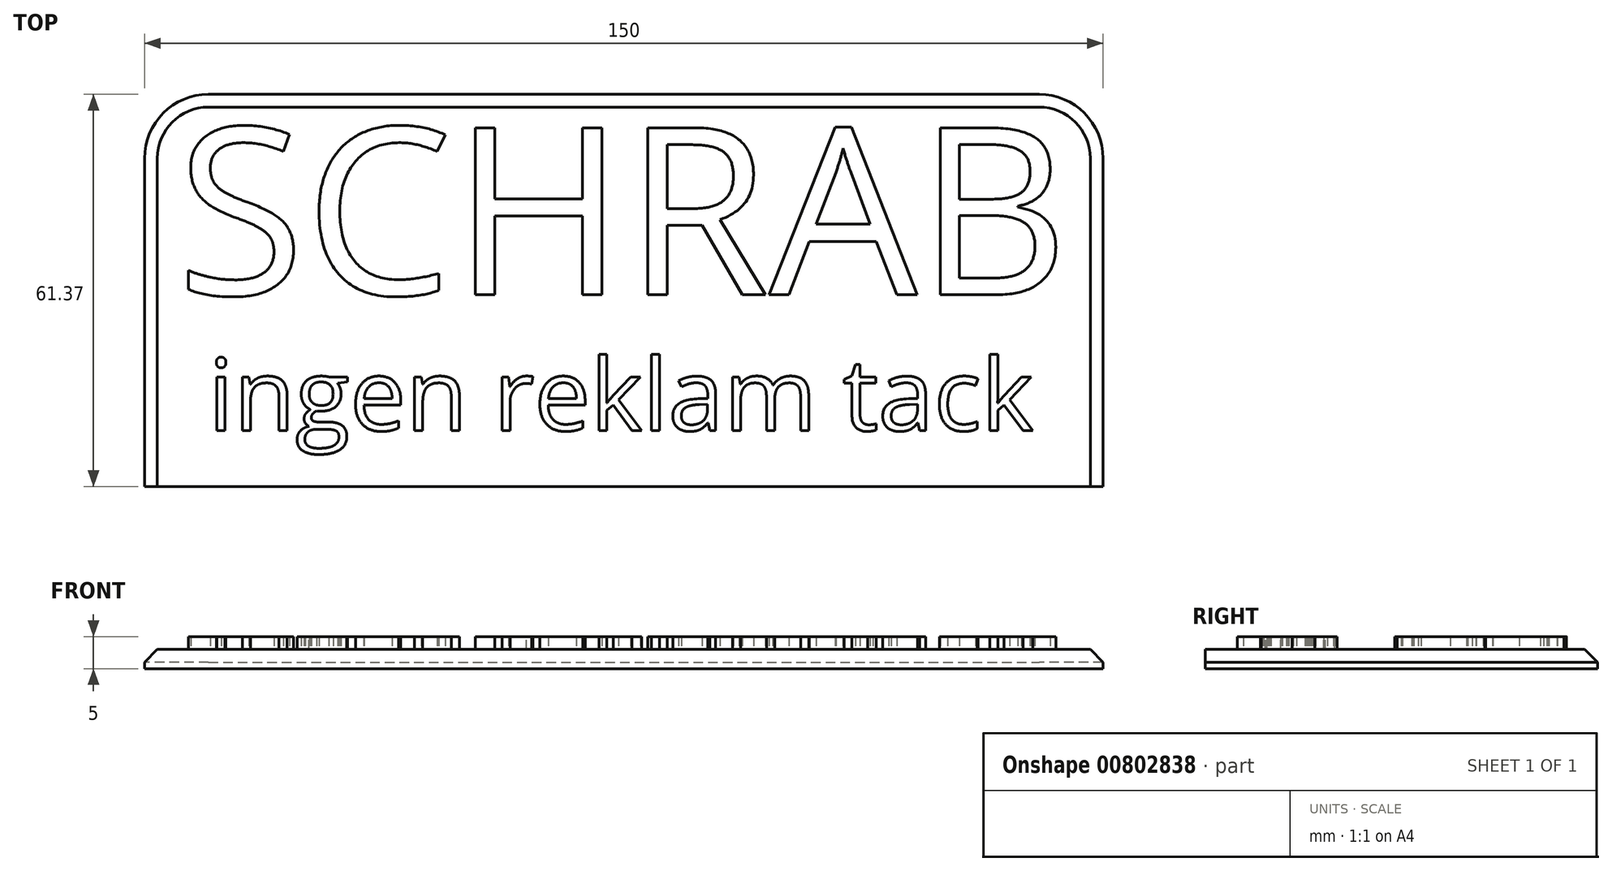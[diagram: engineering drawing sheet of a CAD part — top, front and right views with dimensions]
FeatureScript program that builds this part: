
annotation { "Feature Type Name" : "Feature", "Feature Type Description" : "" }
export const myFeature = defineFeature(function(context is Context, id is Id, definition is map)
    precondition{}
    {
        {
            var Q0;
            Q0=qCreatedBy(makeId("Top.planeOp"),FACE);
            var sketch = newSketch(context, id + "F0", { "sketchPlane" : qUnion([Q0])});
            skLineSegment(sketch, "E0.bottom", {"start": v(-74.1, 45.53) * mm, "end": v(75.9, 45.53) * mm});
            skLineSegment(sketch, "E0.top", {"start": v(-74.1, -34.47) * mm, "end": v(75.9, -34.47) * mm});
            skLineSegment(sketch, "E0.left", {"start": v(-74.1, 45.53) * mm, "end": v(-74.1, -34.47) * mm});
            skLineSegment(sketch, "E0.right", {"start": v(75.9, 45.53) * mm, "end": v(75.9, -34.47) * mm});
            skSolve(sketch);
        }
        {
            var Q0;
            Q0=makeQuery(id+"F0.imprint","IMPRINT",FACE,{"disambiguationData":[TD([[makeQuery(id+"F0.imprint","IMPRINT",EDGE,{"derivedFrom":sQuery(id+"F0.wireOp",EDGE,"E0.bottom")}),-1.0]])]});
            extrude(context, id + "F1", {"entities" : qUnion([Q0]), "depth" : 3 * mm, "offsetDistance" : 25 * mm});
        }
        {
            var Q0;
            Q0=makeQuery(id+"F1.opExtrude","CAP_FACE",FACE,{"disambiguationData":[OSD([sQuery(id+"F0.wireOp",EDGE,"E0.bottom"),sQuery(id+"F0.wireOp",EDGE,"E0.top"),sQuery(id+"F0.wireOp",EDGE,"E0.left"),sQuery(id+"F0.wireOp",EDGE,"E0.right")])],"isStart":false});
            var sketch = newSketch(context, id + "F2", { "sketchPlane" : qUnion([Q0])});
            skText(sketch, "E1", { "text": "SCHRAB", "fontName": "OpenSans-Regular.ttf"});
            skText(sketch, "E2", { "text": "ingen reklam tack", "fontName": "OpenSans-Regular.ttf"});
            const initialGuessF2  = {"E1": [-0.0691, 0.01419, 1, 0, 0.02634], "E2": [-0.0641, -0.00708, 1, 0, 0.01127]};
            skSetInitialGuess(sketch, initialGuessF2);
            skSolve(sketch);
        }
        {
            var Q0;
            Q0 = qSketchRegion(id + "F2", true);
            extrude(context, id + "F3", {"entities" : qUnion([Q0]), "operationType" : NewBodyOperationType.ADD, "depth" : 2 * mm, "offsetDistance" : 25 * mm});
        }
        {
            var Q0;
            {var subQ0=sQuery(id+"F0.wireOp",EDGE,"E0.left");var subQ1=sQuery(id+"F0.wireOp",EDGE,"E0.bottom");var subQ2=sQuery(id+"F0.wireOp",EDGE,"E0.right");var subQ3=sQuery(id+"F0.wireOp",EDGE,"E0.top");Q0=makeQuery(id+"F3.boolean.opBoolean","SPLIT",FACE,{"disambiguationData":[TD([makeQuery(id+"F1.opExtrude","SWEPT_FACE",FACE,{"disambiguationData":[OSD([subQ1])]})])],"derivedFrom":makeQuery(id+"F1.opExtrude","CAP_FACE",FACE,{"disambiguationData":[OSD([subQ1,subQ3,subQ0,subQ2])],"isStart":false})});}
            var sketch = newSketch(context, id + "F4", { "sketchPlane" : qUnion([Q0])});
            skLineSegment(sketch, "E3.bottom", {"start": v(-74.1, -34.47) * mm, "end": v(75.9, -34.47) * mm});
            skLineSegment(sketch, "E3.top", {"start": v(-74.1, -15.84) * mm, "end": v(75.9, -15.84) * mm});
            skLineSegment(sketch, "E3.left", {"start": v(-74.1, -34.47) * mm, "end": v(-74.1, -15.84) * mm});
            skLineSegment(sketch, "E3.right", {"start": v(75.9, -34.47) * mm, "end": v(75.9, -15.84) * mm});
            skSolve(sketch);
        }
        {
            var Q0;
            Q0=makeQuery(id+"F4.imprint","IMPRINT",FACE,{"disambiguationData":[TD([[makeQuery(id+"F4.imprint","IMPRINT",EDGE,{"derivedFrom":sQuery(id+"F4.wireOp",EDGE,"E3.bottom")}),1.0]])]});
            extrude(context, id + "F5", {"entities" : qUnion([Q0]), "operationType" : NewBodyOperationType.REMOVE, "oppositeDirection" : true, "depth" : 25 * mm, "offsetDistance" : 25 * mm});
        }
        {
            var Q0;
            Q0=makeQuery(id+"F1.opExtrude","SWEPT_EDGE",EDGE,{"disambiguationData":[OSD([sQuery(id+"F0.wireOp",EDGE,"E0.bottom"),sQuery(id+"F0.wireOp",EDGE,"E0.right")])]});
            var Q1;
            Q1=makeQuery(id+"F5.boolean.opBoolean","COPY",EDGE,{"derivedFrom":makeQuery(id+"F5.opExtrude","SWEPT_EDGE",EDGE,{"disambiguationData":[OSD([sQuery(id+"F0.wireOp",EDGE,"E0.right"),sQuery(id+"F4.wireOp",EDGE,"E3.top"),sQuery(id+"F4.wireOp",EDGE,"E3.right")])]})});
            var Q2;
            Q2=makeQuery(id+"F1.opExtrude","SWEPT_EDGE",EDGE,{"disambiguationData":[OSD([sQuery(id+"F0.wireOp",EDGE,"E0.bottom"),sQuery(id+"F0.wireOp",EDGE,"E0.left")])]});
            var Q3;
            Q3=makeQuery(id+"F5.boolean.opBoolean","COPY",EDGE,{"derivedFrom":makeQuery(id+"F5.opExtrude","SWEPT_EDGE",EDGE,{"disambiguationData":[OSD([sQuery(id+"F0.wireOp",EDGE,"E0.left"),sQuery(id+"F4.wireOp",EDGE,"E3.top"),sQuery(id+"F4.wireOp",EDGE,"E3.left")])]})});
            fillet(context, id + "F6", {"entities" : qUnion([Q0, Q1, Q2, Q3]), "radius" : 10 * mm, "tangentPropagation" : true, "allowEdgeOverflow" : false});
        }
        {
            var Q0;
            {var subQ0=sQuery(id+"F0.wireOp",EDGE,"E0.left");var subQ1=sQuery(id+"F0.wireOp",EDGE,"E0.bottom");var subQ2=sQuery(id+"F0.wireOp",EDGE,"E0.right");var subQ3=sQuery(id+"F0.wireOp",EDGE,"E0.top");Q0=makeQuery(id+"F6.opFillet","BLEND_EDGE",EDGE,{"blendedFrom":[makeQuery(id+"F1.opExtrude","SWEPT_EDGE",EDGE,{"disambiguationData":[OSD([subQ1,subQ0])]}),makeQuery(id+"F3.boolean.opBoolean","SPLIT",FACE,{"disambiguationData":[TD([makeQuery(id+"F1.opExtrude","SWEPT_FACE",FACE,{"disambiguationData":[OSD([subQ1])]})])],"derivedFrom":makeQuery(id+"F1.opExtrude","CAP_FACE",FACE,{"disambiguationData":[OSD([subQ1,subQ3,subQ0,subQ2])],"isStart":false})})],"blendedInto":[makeQuery(id+"F3.boolean.opBoolean","SPLIT",FACE,{"disambiguationData":[TD([makeQuery(id+"F1.opExtrude","SWEPT_FACE",FACE,{"disambiguationData":[OSD([subQ1])]})])],"derivedFrom":makeQuery(id+"F1.opExtrude","CAP_FACE",FACE,{"disambiguationData":[OSD([subQ1,subQ3,subQ0,subQ2])],"isStart":false})})]});}
            var Q1;
            Q1=makeQuery(id+"F1.opExtrude","CAP_EDGE",EDGE,{"disambiguationData":[OSD([sQuery(id+"F0.wireOp",EDGE,"E0.left")])],"isStart":false});
            var Q2;
            {var subQ0=sQuery(id+"F0.wireOp",EDGE,"E0.left");var subQ1=sQuery(id+"F0.wireOp",EDGE,"E0.bottom");var subQ2=sQuery(id+"F0.wireOp",EDGE,"E0.right");var subQ3=sQuery(id+"F0.wireOp",EDGE,"E0.top");Q2=makeQuery(id+"F6.opFillet","BLEND_EDGE",EDGE,{"blendedFrom":[makeQuery(id+"F5.boolean.opBoolean","COPY",EDGE,{"derivedFrom":makeQuery(id+"F5.opExtrude","SWEPT_EDGE",EDGE,{"disambiguationData":[OSD([subQ0,sQuery(id+"F4.wireOp",EDGE,"E3.top"),sQuery(id+"F4.wireOp",EDGE,"E3.left")])]})}),makeQuery(id+"F3.boolean.opBoolean","SPLIT",FACE,{"disambiguationData":[TD([makeQuery(id+"F1.opExtrude","SWEPT_FACE",FACE,{"disambiguationData":[OSD([subQ1])]})])],"derivedFrom":makeQuery(id+"F1.opExtrude","CAP_FACE",FACE,{"disambiguationData":[OSD([subQ1,subQ3,subQ0,subQ2])],"isStart":false})})],"blendedInto":[makeQuery(id+"F3.boolean.opBoolean","SPLIT",FACE,{"disambiguationData":[TD([makeQuery(id+"F1.opExtrude","SWEPT_FACE",FACE,{"disambiguationData":[OSD([subQ1])]})])],"derivedFrom":makeQuery(id+"F1.opExtrude","CAP_FACE",FACE,{"disambiguationData":[OSD([subQ1,subQ3,subQ0,subQ2])],"isStart":false})})]});}
            var Q3;
            Q3=makeQuery(id+"F5.boolean.opBoolean","COPY",EDGE,{"derivedFrom":makeQuery(id+"F5.opExtrude","CAP_EDGE",EDGE,{"disambiguationData":[OSD([sQuery(id+"F4.wireOp",EDGE,"E3.top")])],"isStart":true})});
            var Q4;
            {var subQ0=sQuery(id+"F0.wireOp",EDGE,"E0.left");var subQ1=sQuery(id+"F0.wireOp",EDGE,"E0.bottom");var subQ2=sQuery(id+"F0.wireOp",EDGE,"E0.right");var subQ3=sQuery(id+"F0.wireOp",EDGE,"E0.top");Q4=makeQuery(id+"F6.opFillet","BLEND_EDGE",EDGE,{"blendedFrom":[makeQuery(id+"F5.boolean.opBoolean","COPY",EDGE,{"derivedFrom":makeQuery(id+"F5.opExtrude","SWEPT_EDGE",EDGE,{"disambiguationData":[OSD([subQ2,sQuery(id+"F4.wireOp",EDGE,"E3.top"),sQuery(id+"F4.wireOp",EDGE,"E3.right")])]})}),makeQuery(id+"F3.boolean.opBoolean","SPLIT",FACE,{"disambiguationData":[TD([makeQuery(id+"F1.opExtrude","SWEPT_FACE",FACE,{"disambiguationData":[OSD([subQ1])]})])],"derivedFrom":makeQuery(id+"F1.opExtrude","CAP_FACE",FACE,{"disambiguationData":[OSD([subQ1,subQ3,subQ0,subQ2])],"isStart":false})})],"blendedInto":[makeQuery(id+"F3.boolean.opBoolean","SPLIT",FACE,{"disambiguationData":[TD([makeQuery(id+"F1.opExtrude","SWEPT_FACE",FACE,{"disambiguationData":[OSD([subQ1])]})])],"derivedFrom":makeQuery(id+"F1.opExtrude","CAP_FACE",FACE,{"disambiguationData":[OSD([subQ1,subQ3,subQ0,subQ2])],"isStart":false})})]});}
            var Q5;
            Q5=makeQuery(id+"F1.opExtrude","CAP_EDGE",EDGE,{"disambiguationData":[OSD([sQuery(id+"F0.wireOp",EDGE,"E0.right")])],"isStart":false});
            var Q6;
            {var subQ0=sQuery(id+"F0.wireOp",EDGE,"E0.left");var subQ1=sQuery(id+"F0.wireOp",EDGE,"E0.bottom");var subQ2=sQuery(id+"F0.wireOp",EDGE,"E0.right");var subQ3=sQuery(id+"F0.wireOp",EDGE,"E0.top");Q6=makeQuery(id+"F6.opFillet","BLEND_EDGE",EDGE,{"blendedFrom":[makeQuery(id+"F1.opExtrude","SWEPT_EDGE",EDGE,{"disambiguationData":[OSD([subQ1,subQ2])]}),makeQuery(id+"F3.boolean.opBoolean","SPLIT",FACE,{"disambiguationData":[TD([makeQuery(id+"F1.opExtrude","SWEPT_FACE",FACE,{"disambiguationData":[OSD([subQ1])]})])],"derivedFrom":makeQuery(id+"F1.opExtrude","CAP_FACE",FACE,{"disambiguationData":[OSD([subQ1,subQ3,subQ0,subQ2])],"isStart":false})})],"blendedInto":[makeQuery(id+"F3.boolean.opBoolean","SPLIT",FACE,{"disambiguationData":[TD([makeQuery(id+"F1.opExtrude","SWEPT_FACE",FACE,{"disambiguationData":[OSD([subQ1])]})])],"derivedFrom":makeQuery(id+"F1.opExtrude","CAP_FACE",FACE,{"disambiguationData":[OSD([subQ1,subQ3,subQ0,subQ2])],"isStart":false})})]});}
            var Q7;
            Q7=makeQuery(id+"F1.opExtrude","CAP_EDGE",EDGE,{"disambiguationData":[OSD([sQuery(id+"F0.wireOp",EDGE,"E0.bottom")])],"isStart":false});
            chamfer(context, id + "F7", {"entities" : qUnion([Q0, Q1, Q2, Q3, Q4, Q5, Q6, Q7]), "width" : 2 * mm, "tangentPropagation" : true});
        }
    });
